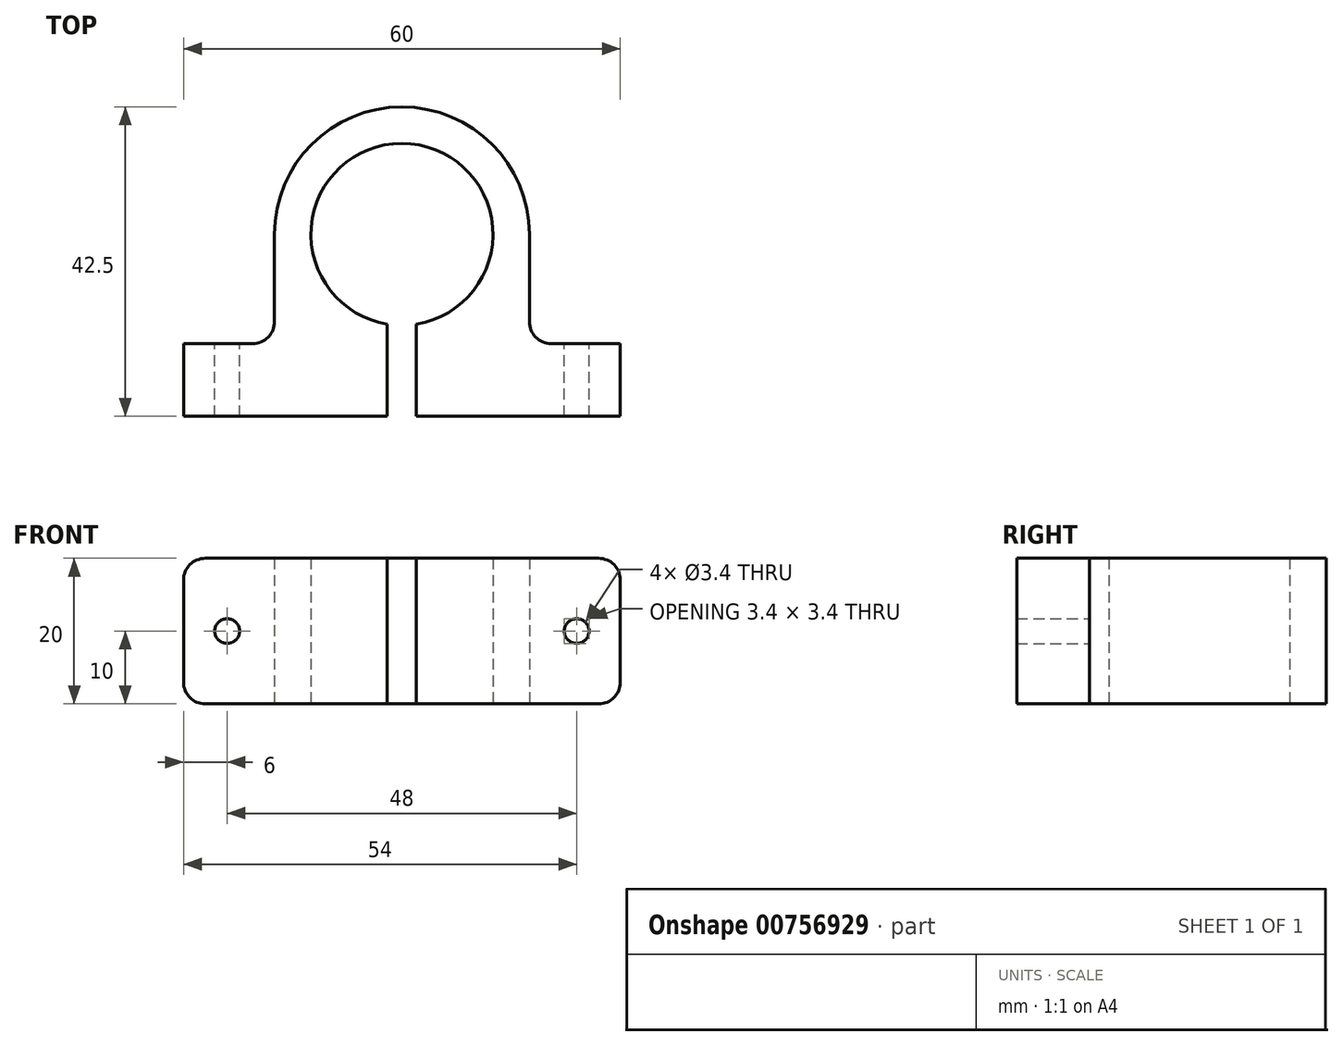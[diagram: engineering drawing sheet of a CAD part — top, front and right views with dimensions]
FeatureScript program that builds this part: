
annotation { "Feature Type Name" : "Feature", "Feature Type Description" : "" }
export const myFeature = defineFeature(function(context is Context, id is Id, definition is map)
    precondition{}
    {
        {
            var Q0;
            Q0=qCreatedBy(makeId("Top.planeOp"),FACE);
            var sketch = newSketch(context, id + "F0", { "sketchPlane" : qUnion([Q0])});
            skArc(sketch, "E0", {"start": v(2, -12.34) * mm, "mid": v(0, 12.5) * mm, "end": v(-2, -12.34) * mm});
            skArc(sketch, "E1", {"start": v(17.5, 0) * mm, "mid": v(0, 17.5) * mm, "end": v(-17.5, 0) * mm});
            skLineSegment(sketch, "E2", {"start": v(17.5, 0) * mm, "end": v(17.5, -15) * mm});
            skLineSegment(sketch, "E3", {"start": v(17.5, -15) * mm, "end": v(30, -15) * mm});
            skLineSegment(sketch, "E4", {"start": v(30, -15) * mm, "end": v(30, -25) * mm});
            skLineSegment(sketch, "E5", {"start": v(30, -25) * mm, "end": v(2, -25) * mm});
            skLineSegment(sketch, "E6", {"start": v(2, -25) * mm, "end": v(2, -12.34) * mm});
            skLineSegment(sketch, "E7.MirrorCS", {"start": v(-2, -25) * mm, "end": v(-2, -12.34) * mm});
            skLineSegment(sketch, "E8.MirrorCS", {"start": v(-30, -25) * mm, "end": v(-2, -25) * mm});
            skLineSegment(sketch, "E9.MirrorCS", {"start": v(-30, -15) * mm, "end": v(-30, -25) * mm});
            skLineSegment(sketch, "E10.MirrorCS", {"start": v(-17.5, -15) * mm, "end": v(-30, -15) * mm});
            skLineSegment(sketch, "E11.MirrorCS", {"start": v(-17.5, 0) * mm, "end": v(-17.5, -15) * mm});
            skSolve(sketch);
        }
        {
            var Q0;
            Q0=makeQuery(id+"F0.imprint","IMPRINT",FACE,{"disambiguationData":[TD([[makeQuery(id+"F0.imprint","IMPRINT",EDGE,{"derivedFrom":sQuery(id+"F0.wireOp",EDGE,"E0")}),-1.0]])]});
            extrude(context, id + "F1", {"entities" : qUnion([Q0]), "endBound" : BoundingType.SYMMETRIC, "depth" : 20 * mm, "offsetDistance" : 25 * mm});
        }
        {
            var Q0;
            Q0=makeQuery(id+"F1.opExtrude","SWEPT_FACE",FACE,{"disambiguationData":[OSD([sQuery(id+"F0.wireOp",EDGE,"E3")])]});
            var sketch = newSketch(context, id + "F2", { "sketchPlane" : qUnion([Q0])});
            skPoint(sketch, "E12", {"position": v(-24, 0) * mm});
            skPoint(sketch, "E13", {"position": v(24, 0) * mm});
            skSolve(sketch);
        }
        {
            var Q0;
            Q0=sQuery(id+"F2.wireOp",VERTEX,"E13");
            var Q1;
            Q1=sQuery(id+"F2.wireOp",VERTEX,"E12");
            var Q2;
            Q2=makeQuery(id+"F1.opExtrude","SWEPT_BODY",BODY,{"disambiguationData":[OSD([sQuery(id+"F0.wireOp",EDGE,"E0"),sQuery(id+"F0.wireOp",EDGE,"E1"),sQuery(id+"F0.wireOp",EDGE,"E2"),sQuery(id+"F0.wireOp",EDGE,"E3"),sQuery(id+"F0.wireOp",EDGE,"E4"),sQuery(id+"F0.wireOp",EDGE,"E5"),sQuery(id+"F0.wireOp",EDGE,"E6"),sQuery(id+"F0.wireOp",EDGE,"E7.MirrorCS"),sQuery(id+"F0.wireOp",EDGE,"E8.MirrorCS"),sQuery(id+"F0.wireOp",EDGE,"E9.MirrorCS"),sQuery(id+"F0.wireOp",EDGE,"E10.MirrorCS"),sQuery(id+"F0.wireOp",EDGE,"E11.MirrorCS")])]});
            hole(context, id + "F3", {"style" : HoleStyle.SIMPLE, "endStyle" : HoleEndStyle.THROUGH, "holeDiameter" : 3.4 * mm, "majorDiameter" : 5 * mm, "isTappedThrough" : true, "tappedDepth" : 12 * mm, "tapClearance" : 3, "locations" : qUnion([Q0, Q1]), "scope" : qUnion([Q2])});
        }
        {
            var Q0;
            Q0=makeQuery(id+"F1.opExtrude","SWEPT_EDGE",EDGE,{"disambiguationData":[OSD([sQuery(id+"F0.wireOp",EDGE,"E2"),sQuery(id+"F0.wireOp",EDGE,"E3")])]});
            var Q1;
            Q1=makeQuery(id+"F1.opExtrude","SWEPT_EDGE",EDGE,{"disambiguationData":[OSD([sQuery(id+"F0.wireOp",EDGE,"E10.MirrorCS"),sQuery(id+"F0.wireOp",EDGE,"E11.MirrorCS")])]});
            var Q2;
            Q2=makeQuery(id+"F1.opExtrude","CAP_EDGE",EDGE,{"disambiguationData":[OSD([sQuery(id+"F0.wireOp",EDGE,"E9.MirrorCS")])],"isStart":false});
            var Q3;
            Q3=makeQuery(id+"F1.opExtrude","CAP_EDGE",EDGE,{"disambiguationData":[OSD([sQuery(id+"F0.wireOp",EDGE,"E9.MirrorCS")])],"isStart":true});
            var Q4;
            Q4=makeQuery(id+"F1.opExtrude","CAP_EDGE",EDGE,{"disambiguationData":[OSD([sQuery(id+"F0.wireOp",EDGE,"E4")])],"isStart":false});
            var Q5;
            Q5=makeQuery(id+"F1.opExtrude","CAP_EDGE",EDGE,{"disambiguationData":[OSD([sQuery(id+"F0.wireOp",EDGE,"E4")])],"isStart":true});
            fillet(context, id + "F4", {"entities" : qUnion([Q0, Q1, Q2, Q3, Q4, Q5]), "radius" : 3 * mm, "tangentPropagation" : true, "allowEdgeOverflow" : false});
        }
    });
